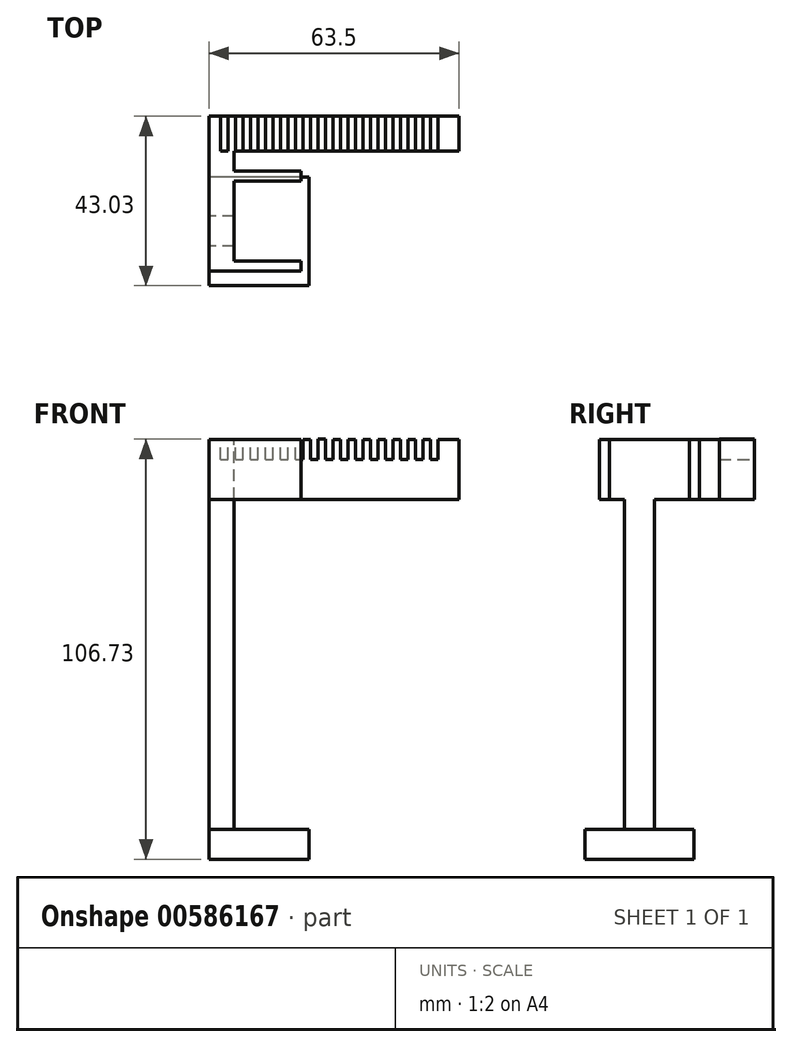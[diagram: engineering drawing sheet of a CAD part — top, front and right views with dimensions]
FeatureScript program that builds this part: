
annotation { "Feature Type Name" : "Feature", "Feature Type Description" : "" }
export const myFeature = defineFeature(function(context is Context, id is Id, definition is map)
    precondition{}
    {
        {
            var Q0;
            Q0=qCreatedBy(makeId("Front.planeOp"),FACE);
            var sketch = newSketch(context, id + "F0", { "sketchPlane" : qUnion([Q0])});
            skLineSegment(sketch, "E0.bottom", {"start": v(-64.89, 15.49) * mm, "end": v(-1.39, 15.49) * mm});
            skLineSegment(sketch, "E0.top", {"start": v(-64.89, 5.33) * mm, "end": v(-1.39, 5.33) * mm});
            skLineSegment(sketch, "E0.left", {"start": v(-64.89, 15.49) * mm, "end": v(-64.89, 5.33) * mm});
            skLineSegment(sketch, "E0.right", {"start": v(-1.39, 15.49) * mm, "end": v(-1.39, 5.33) * mm});
            skLineSegment(sketch, "E1.bottom", {"start": v(-1.39, 15.49) * mm, "end": v(-13.31, 15.49) * mm});
            skLineSegment(sketch, "E1.top", {"start": v(-11.73, 20.57) * mm, "end": v(-13.31, 20.57) * mm});
            skLineSegment(sketch, "E2.bottom", {"start": v(-48.7, 15.49) * mm, "end": v(-46.79, 15.49) * mm});
            skLineSegment(sketch, "E2.top", {"start": v(-48.7, 20.57) * mm, "end": v(-46.79, 20.57) * mm});
            skLineSegment(sketch, "E2.left", {"start": v(-48.7, 15.49) * mm, "end": v(-48.7, 20.57) * mm});
            skLineSegment(sketch, "E2.right", {"start": v(-46.79, 15.49) * mm, "end": v(-46.79, 20.57) * mm});
            skLineSegment(sketch, "E3.bottom", {"start": v(-44.88, 15.49) * mm, "end": v(-42.98, 15.49) * mm});
            skLineSegment(sketch, "E3.top", {"start": v(-44.88, 20.57) * mm, "end": v(-42.98, 20.57) * mm});
            skLineSegment(sketch, "E3.left", {"start": v(-44.88, 15.49) * mm, "end": v(-44.88, 20.57) * mm});
            skLineSegment(sketch, "E3.right", {"start": v(-42.98, 15.49) * mm, "end": v(-42.98, 20.57) * mm});
            skLineSegment(sketch, "E4.bottom", {"start": v(-41.07, 15.49) * mm, "end": v(-39.17, 15.49) * mm});
            skLineSegment(sketch, "E4.top", {"start": v(-41.07, 20.57) * mm, "end": v(-39.17, 20.57) * mm});
            skLineSegment(sketch, "E4.left", {"start": v(-41.07, 15.49) * mm, "end": v(-41.07, 20.57) * mm});
            skLineSegment(sketch, "E4.right", {"start": v(-39.17, 15.49) * mm, "end": v(-39.17, 20.57) * mm});
            skLineSegment(sketch, "E5.bottom", {"start": v(-37.26, 15.49) * mm, "end": v(-35.36, 15.49) * mm});
            skLineSegment(sketch, "E5.top", {"start": v(-37.26, 20.62) * mm, "end": v(-35.36, 20.62) * mm});
            skLineSegment(sketch, "E5.left", {"start": v(-37.26, 15.49) * mm, "end": v(-37.26, 20.62) * mm});
            skLineSegment(sketch, "E5.right", {"start": v(-35.36, 15.49) * mm, "end": v(-35.36, 20.62) * mm});
            skLineSegment(sketch, "E6.bottom", {"start": v(-33.45, 15.49) * mm, "end": v(-31.55, 15.49) * mm});
            skLineSegment(sketch, "E6.top", {"start": v(-33.45, 20.57) * mm, "end": v(-31.55, 20.57) * mm});
            skLineSegment(sketch, "E6.left", {"start": v(-33.45, 15.49) * mm, "end": v(-33.45, 20.57) * mm});
            skLineSegment(sketch, "E6.right", {"start": v(-31.55, 15.49) * mm, "end": v(-31.55, 20.57) * mm});
            skLineSegment(sketch, "E7.bottom", {"start": v(-29.64, 15.49) * mm, "end": v(-27.74, 15.49) * mm});
            skLineSegment(sketch, "E7.top", {"start": v(-29.64, 20.57) * mm, "end": v(-27.74, 20.57) * mm});
            skLineSegment(sketch, "E7.left", {"start": v(-29.64, 15.49) * mm, "end": v(-29.64, 20.57) * mm});
            skLineSegment(sketch, "E7.right", {"start": v(-27.74, 15.49) * mm, "end": v(-27.74, 20.57) * mm});
            skLineSegment(sketch, "E8.bottom", {"start": v(-25.83, 15.49) * mm, "end": v(-23.93, 15.49) * mm});
            skLineSegment(sketch, "E8.top", {"start": v(-25.83, 20.57) * mm, "end": v(-23.93, 20.57) * mm});
            skLineSegment(sketch, "E8.left", {"start": v(-25.83, 15.49) * mm, "end": v(-25.83, 20.57) * mm});
            skLineSegment(sketch, "E8.right", {"start": v(-23.93, 15.49) * mm, "end": v(-23.93, 20.57) * mm});
            skLineSegment(sketch, "E9.bottom", {"start": v(-22.02, 15.49) * mm, "end": v(-20.12, 15.49) * mm});
            skLineSegment(sketch, "E9.top", {"start": v(-22.02, 20.57) * mm, "end": v(-20.12, 20.57) * mm});
            skLineSegment(sketch, "E9.left", {"start": v(-22.02, 15.49) * mm, "end": v(-22.02, 20.57) * mm});
            skLineSegment(sketch, "E9.right", {"start": v(-20.12, 15.49) * mm, "end": v(-20.12, 20.57) * mm});
            skLineSegment(sketch, "E10.bottom", {"start": v(-18.21, 15.49) * mm, "end": v(-16.3, 15.49) * mm});
            skLineSegment(sketch, "E10.top", {"start": v(-18.21, 20.57) * mm, "end": v(-16.3, 20.57) * mm});
            skLineSegment(sketch, "E10.left", {"start": v(-18.21, 15.49) * mm, "end": v(-18.21, 20.57) * mm});
            skLineSegment(sketch, "E10.right", {"start": v(-16.3, 15.49) * mm, "end": v(-16.3, 20.57) * mm});
            skLineSegment(sketch, "E11.bottom", {"start": v(-8.69, 15.49) * mm, "end": v(-10.6, 15.49) * mm});
            skLineSegment(sketch, "E11.top", {"start": v(-8.69, 20.57) * mm, "end": v(-10.6, 20.57) * mm});
            skLineSegment(sketch, "E11.left", {"start": v(-8.69, 15.49) * mm, "end": v(-8.69, 20.57) * mm});
            skLineSegment(sketch, "E11.right", {"start": v(-10.6, 15.49) * mm, "end": v(-10.6, 20.57) * mm});
            skLineSegment(sketch, "E12.bottom", {"start": v(-14.4, 15.49) * mm, "end": v(-12.5, 15.49) * mm});
            skLineSegment(sketch, "E12.top", {"start": v(-14.4, 20.57) * mm, "end": v(-12.5, 20.57) * mm});
            skLineSegment(sketch, "E12.left", {"start": v(-14.4, 15.49) * mm, "end": v(-14.4, 20.57) * mm});
            skLineSegment(sketch, "E12.right", {"start": v(-12.5, 15.49) * mm, "end": v(-12.5, 20.57) * mm});
            skLineSegment(sketch, "E13.bottom", {"start": v(-6.78, 15.49) * mm, "end": v(-1.39, 15.49) * mm});
            skLineSegment(sketch, "E13.top", {"start": v(-6.78, 20.57) * mm, "end": v(-1.39, 20.57) * mm});
            skLineSegment(sketch, "E13.left", {"start": v(-6.78, 15.49) * mm, "end": v(-6.78, 20.57) * mm});
            skLineSegment(sketch, "E13.right", {"start": v(-1.39, 15.49) * mm, "end": v(-1.39, 20.57) * mm});
            skLineSegment(sketch, "E14.bottom", {"start": v(-50.6, 15.49) * mm, "end": v(-52.5, 15.49) * mm});
            skLineSegment(sketch, "E14.top", {"start": v(-50.6, 20.57) * mm, "end": v(-52.5, 20.57) * mm});
            skLineSegment(sketch, "E14.left", {"start": v(-50.6, 15.49) * mm, "end": v(-50.6, 20.57) * mm});
            skLineSegment(sketch, "E14.right", {"start": v(-52.5, 15.49) * mm, "end": v(-52.5, 20.57) * mm});
            skLineSegment(sketch, "E15.bottom", {"start": v(-54.4, 15.49) * mm, "end": v(-56.31, 15.49) * mm});
            skLineSegment(sketch, "E15.top", {"start": v(-54.4, 20.57) * mm, "end": v(-56.31, 20.57) * mm});
            skLineSegment(sketch, "E15.left", {"start": v(-54.4, 15.49) * mm, "end": v(-54.4, 20.57) * mm});
            skLineSegment(sketch, "E15.right", {"start": v(-56.31, 15.49) * mm, "end": v(-56.31, 20.57) * mm});
            skLineSegment(sketch, "E16.bottom", {"start": v(-58.22, 15.49) * mm, "end": v(-60.12, 15.49) * mm});
            skLineSegment(sketch, "E16.top", {"start": v(-58.22, 20.57) * mm, "end": v(-60.12, 20.57) * mm});
            skLineSegment(sketch, "E16.left", {"start": v(-58.22, 15.49) * mm, "end": v(-58.22, 20.57) * mm});
            skLineSegment(sketch, "E16.right", {"start": v(-60.12, 15.49) * mm, "end": v(-60.12, 20.57) * mm});
            skLineSegment(sketch, "E17.bottom", {"start": v(-64.89, 15.49) * mm, "end": v(-62.03, 15.49) * mm});
            skLineSegment(sketch, "E17.top", {"start": v(-64.89, 20.57) * mm, "end": v(-62.03, 20.57) * mm});
            skLineSegment(sketch, "E17.left", {"start": v(-64.89, 15.49) * mm, "end": v(-64.89, 20.57) * mm});
            skLineSegment(sketch, "E17.right", {"start": v(-62.03, 15.49) * mm, "end": v(-62.03, 20.57) * mm});
            skSolve(sketch);
        }
        {
            var Q0;
            Q0=qSketchRegion(id+"F0",true);
            extrude(context, id + "F1", {"entities" : qUnion([Q0]), "endBound" : BoundingType.SYMMETRIC, "depth" : 8.9 * mm, "offsetDistance" : 25.4 * mm});
        }
        {
            var Q0;
            Q0=makeQuery(id+"F1.opExtrude","SWEPT_FACE",FACE,{"disambiguationData":[OSD([sQuery(id+"F0.wireOp",EDGE,"E0.left"),sQuery(id+"F0.wireOp",EDGE,"E17.left")])]});
            var sketch = newSketch(context, id + "F2", { "sketchPlane" : qUnion([Q0])});
            skLineSegment(sketch, "E18.bottom", {"start": v(4.45, 20.57) * mm, "end": v(34.92, 20.57) * mm});
            skLineSegment(sketch, "E18.top", {"start": v(4.45, 5.33) * mm, "end": v(34.92, 5.33) * mm});
            skLineSegment(sketch, "E18.left", {"start": v(4.45, 20.57) * mm, "end": v(4.45, 5.33) * mm});
            skLineSegment(sketch, "E18.right", {"start": v(34.92, 20.57) * mm, "end": v(34.92, 5.33) * mm});
            skSolve(sketch);
        }
        {
            var Q0;
            Q0=makeQuery(id+"F2.imprint","IMPRINT",FACE,{"disambiguationData":[TD([[makeQuery(id+"F2.imprint","IMPRINT",EDGE,{"derivedFrom":sQuery(id+"F2.wireOp",EDGE,"E18.bottom")}),-1.0]])]});
            extrude(context, id + "F3", {"entities" : qUnion([Q0]), "operationType" : NewBodyOperationType.ADD, "oppositeDirection" : true, "depth" : 6.35 * mm, "offsetDistance" : 25.4 * mm});
        }
        {
            var Q0;
            Q0=makeQuery(id+"F3.boolean.opBoolean","MERGE",FACE,{"derivedFrom":[makeQuery(id+"F1.opExtrude","SWEPT_FACE",FACE,{"disambiguationData":[OSD([sQuery(id+"F0.wireOp",EDGE,"E16.top")])]}),makeQuery(id+"F1.opExtrude","SWEPT_FACE",FACE,{"disambiguationData":[OSD([sQuery(id+"F0.wireOp",EDGE,"E17.top")])]}),makeQuery(id+"F3.opExtrude","SWEPT_FACE",FACE,{"disambiguationData":[OSD([sQuery(id+"F2.wireOp",EDGE,"E18.bottom")])]})]});
            var sketch = newSketch(context, id + "F4", { "sketchPlane" : qUnion([Q0])});
            skLineSegment(sketch, "E19.bottom", {"start": v(-58.54, -34.92) * mm, "end": v(-41.52, -34.92) * mm});
            skLineSegment(sketch, "E19.top", {"start": v(-58.54, -32.38) * mm, "end": v(-41.52, -32.38) * mm});
            skLineSegment(sketch, "E19.left", {"start": v(-58.54, -34.92) * mm, "end": v(-58.54, -32.38) * mm});
            skLineSegment(sketch, "E19.right", {"start": v(-41.52, -34.92) * mm, "end": v(-41.52, -32.38) * mm});
            skLineSegment(sketch, "E20.bottom", {"start": v(-58.54, -12.06) * mm, "end": v(-41.52, -12.06) * mm});
            skLineSegment(sketch, "E20.top", {"start": v(-58.54, -9.52) * mm, "end": v(-41.52, -9.52) * mm});
            skLineSegment(sketch, "E20.left", {"start": v(-58.54, -12.06) * mm, "end": v(-58.54, -9.52) * mm});
            skLineSegment(sketch, "E20.right", {"start": v(-41.52, -12.06) * mm, "end": v(-41.52, -9.52) * mm});
            skLineSegment(sketch, "E21.bottom", {"start": v(-41.52, -32.38) * mm, "end": v(-44.06, -32.38) * mm});
            skLineSegment(sketch, "E21.top", {"start": v(-41.52, -29.84) * mm, "end": v(-44.06, -29.84) * mm});
            skLineSegment(sketch, "E21.left", {"start": v(-41.52, -32.38) * mm, "end": v(-41.52, -29.84) * mm});
            skLineSegment(sketch, "E21.right", {"start": v(-44.06, -32.38) * mm, "end": v(-44.06, -29.84) * mm});
            skSolve(sketch);
        }
        {
            var Q0;
            Q0=makeQuery(id+"F4.imprint","IMPRINT",FACE,{"disambiguationData":[TD([[makeQuery(id+"F4.imprint","IMPRINT",EDGE,{"derivedFrom":sQuery(id+"F4.wireOp",EDGE,"E20.bottom")}),1.0]])]});
            var Q1;
            Q1=makeQuery(id+"F4.imprint","IMPRINT",FACE,{"disambiguationData":[TD([[makeQuery(id+"F4.imprint","IMPRINT",EDGE,{"derivedFrom":sQuery(id+"F4.wireOp",EDGE,"E19.bottom")}),1.0]])]});
            var Q2;
            Q2=makeQuery(id+"F4.imprint","IMPRINT",FACE,{"disambiguationData":[TD([[makeQuery(id+"F4.imprint","IMPRINT",EDGE,{"derivedFrom":sQuery(id+"F4.wireOp",EDGE,"E21.bottom")}),-1.0]])]});
            extrude(context, id + "F5", {"entities" : qUnion([Q0, Q1, Q2]), "operationType" : NewBodyOperationType.ADD, "oppositeDirection" : true, "depth" : 15.24 * mm, "offsetDistance" : 25.4 * mm});
        }
        {
            var Q0;
            Q0=makeQuery(id+"F3.boolean.opBoolean","MERGE",FACE,{"derivedFrom":[makeQuery(id+"F1.opExtrude","SWEPT_FACE",FACE,{"disambiguationData":[OSD([sQuery(id+"F0.wireOp",EDGE,"E0.left"),sQuery(id+"F0.wireOp",EDGE,"E17.left")])]}),makeQuery(id+"F3.opExtrude","CAP_FACE",FACE,{"disambiguationData":[OSD([sQuery(id+"F2.wireOp",EDGE,"E18.bottom"),sQuery(id+"F2.wireOp",EDGE,"E18.top"),sQuery(id+"F2.wireOp",EDGE,"E18.left"),sQuery(id+"F2.wireOp",EDGE,"E18.right")])],"isStart":true})]});
            var sketch = newSketch(context, id + "F6", { "sketchPlane" : qUnion([Q0])});
            skLineSegment(sketch, "E22.bottom", {"start": v(20.95, 5.33) * mm, "end": v(28.57, 5.33) * mm});
            skLineSegment(sketch, "E22.top", {"start": v(20.96, -78.5) * mm, "end": v(28.58, -78.5) * mm});
            skLineSegment(sketch, "E22.left", {"start": v(20.95, 5.33) * mm, "end": v(20.96, -78.5) * mm});
            skLineSegment(sketch, "E22.right", {"start": v(28.57, 5.33) * mm, "end": v(28.58, -78.5) * mm});
            skLineSegment(sketch, "E23.bottom", {"start": v(38.58, -78.5) * mm, "end": v(10.95, -78.5) * mm});
            skLineSegment(sketch, "E23.top", {"start": v(38.58, -86.11) * mm, "end": v(10.95, -86.11) * mm});
            skLineSegment(sketch, "E23.left", {"start": v(38.58, -78.5) * mm, "end": v(38.58, -86.11) * mm});
            skLineSegment(sketch, "E23.right", {"start": v(10.95, -78.5) * mm, "end": v(10.95, -86.11) * mm});
            skPoint(sketch, "E23.middle", {"position": v(24.76, -82.3) * mm});
            skSolve(sketch);
        }
        {
            var Q0;
            Q0=makeQuery(id+"F6.imprint","IMPRINT",FACE,{"disambiguationData":[TD([[makeQuery(id+"F6.imprint","IMPRINT",EDGE,{"derivedFrom":sQuery(id+"F6.wireOp",EDGE,"E22.bottom")}),1.0]])]});
            extrude(context, id + "F7", {"entities" : qUnion([Q0]), "operationType" : NewBodyOperationType.ADD, "oppositeDirection" : true, "depth" : 6.35 * mm, "offsetDistance" : 25.4 * mm});
        }
        {
            var Q0;
            Q0=makeQuery(id+"F6.imprint","IMPRINT",FACE,{"disambiguationData":[TD([[makeQuery(id+"F6.imprint","IMPRINT",EDGE,{"derivedFrom":sQuery(id+"F6.wireOp",EDGE,"E23.top")}),-1.0]])]});
            extrude(context, id + "F8", {"entities" : qUnion([Q0]), "oppositeDirection" : true, "depth" : 25.4 * mm, "offsetDistance" : 25.4 * mm});
        }
    });
